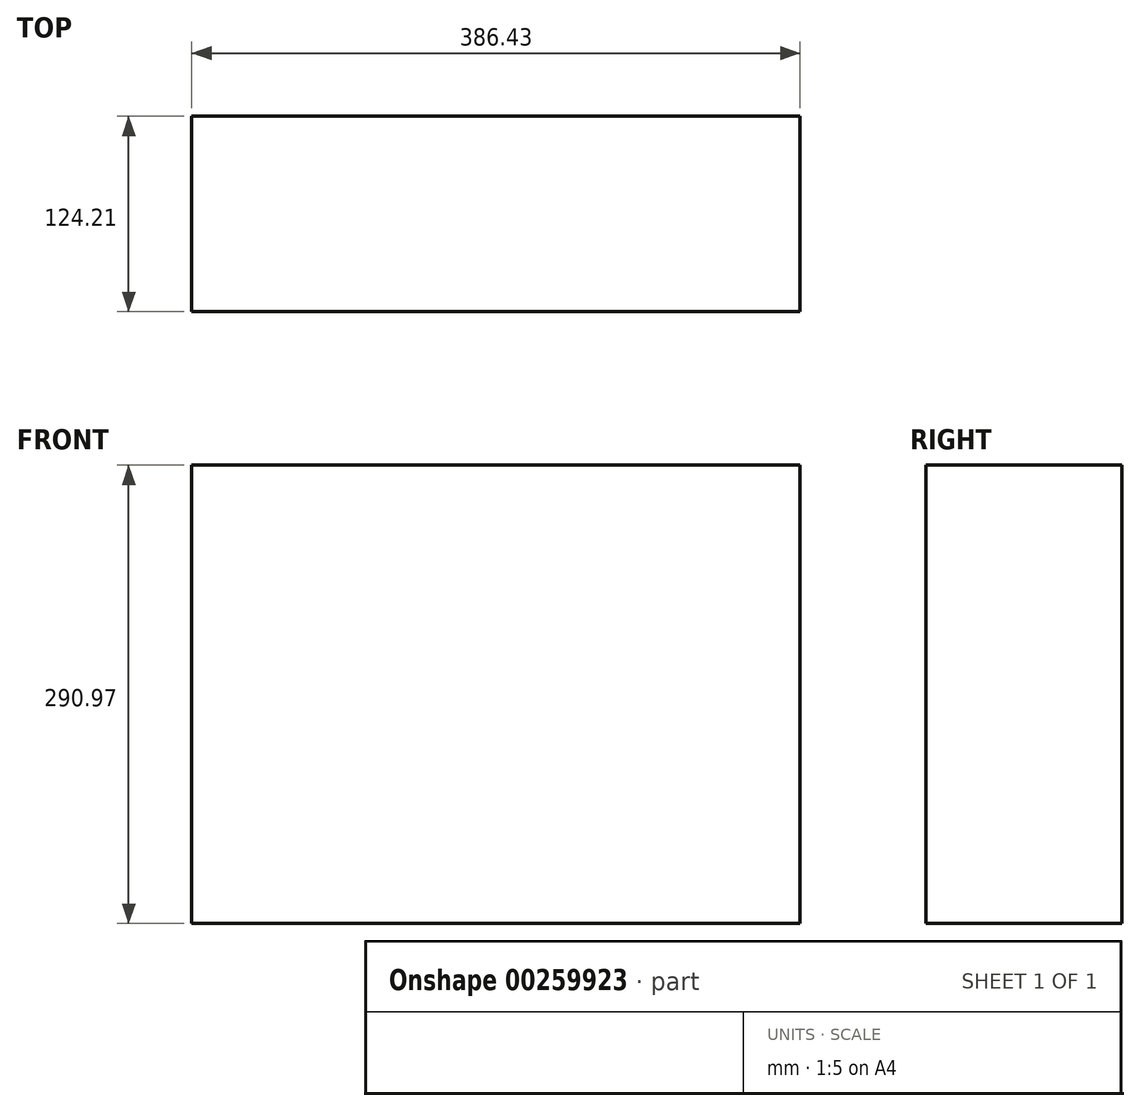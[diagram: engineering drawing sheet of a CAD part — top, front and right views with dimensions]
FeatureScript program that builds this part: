
annotation { "Feature Type Name" : "Feature", "Feature Type Description" : "" }
export const myFeature = defineFeature(function(context is Context, id is Id, definition is map)
    precondition{}
    {
        {
            var Q0;
            Q0=qCreatedBy(makeId("Front.planeOp"),FACE);
            var sketch = newSketch(context, id + "F0", { "sketchPlane" : qUnion([Q0])});
            skLineSegment(sketch, "E0.bottom", {"start": v(0, 0) * mm, "end": v(386.43, 0) * mm});
            skLineSegment(sketch, "E0.top", {"start": v(0, 290.97) * mm, "end": v(386.43, 290.97) * mm});
            skLineSegment(sketch, "E0.left", {"start": v(0, 0) * mm, "end": v(0, 290.97) * mm});
            skLineSegment(sketch, "E0.right", {"start": v(386.43, 0) * mm, "end": v(386.43, 290.97) * mm});
            skSolve(sketch);
        }
        {
            var Q0;
            Q0 = qSketchRegion(id + "F0", true);
            extrude(context, id + "F1", {"entities" : qUnion([Q0]), "depth" : 124.2 * mm});
        }
    });
